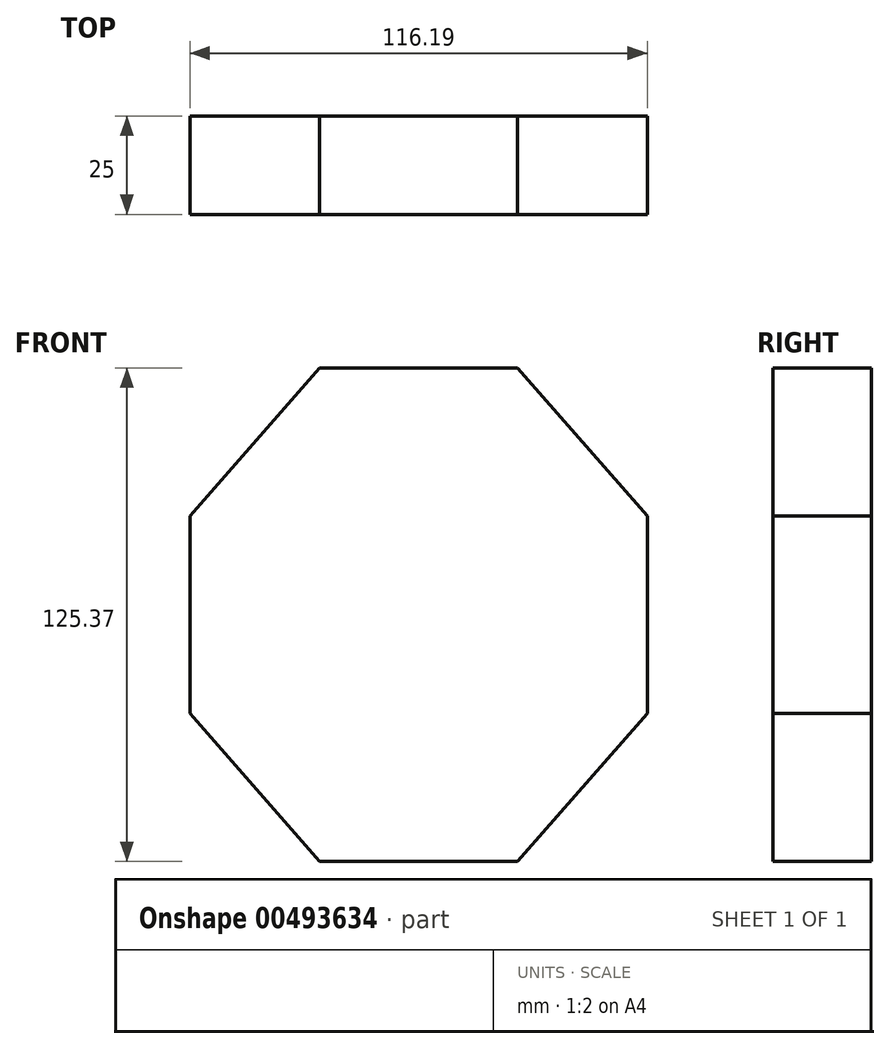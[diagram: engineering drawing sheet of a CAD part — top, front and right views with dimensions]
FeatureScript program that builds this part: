
annotation { "Feature Type Name" : "Feature", "Feature Type Description" : "" }
export const myFeature = defineFeature(function(context is Context, id is Id, definition is map)
    precondition{}
    {
        {
            var Q0;
            Q0=qCreatedBy(makeId("Front.planeOp"),FACE);
            var sketch = newSketch(context, id + "F0", { "sketchPlane" : qUnion([Q0])});
            skLineSegment(sketch, "E0", {"start": v(-37.3, 52.64) * mm, "end": v(12.9, 52.64) * mm});
            skLineSegment(sketch, "E1", {"start": v(12.9, 52.64) * mm, "end": v(45.9, 15.06) * mm});
            skLineSegment(sketch, "E2", {"start": v(45.9, 15.06) * mm, "end": v(45.9, -35.14) * mm});
            skLineSegment(sketch, "E3", {"start": v(45.9, -35.14) * mm, "end": v(12.9, -72.73) * mm});
            skLineSegment(sketch, "E4", {"start": v(12.9, -72.73) * mm, "end": v(-37.3, -72.73) * mm});
            skLineSegment(sketch, "E5", {"start": v(-37.3, -72.73) * mm, "end": v(-70.29, -35.14) * mm});
            skLineSegment(sketch, "E6", {"start": v(-70.29, -35.14) * mm, "end": v(-70.29, 15.06) * mm});
            skLineSegment(sketch, "E7", {"start": v(-70.29, 15.06) * mm, "end": v(-37.3, 52.64) * mm});
            skSolve(sketch);
        }
        {
            var Q0;
            Q0 = qSketchRegion(id + "F0", true);
            extrude(context, id + "F1", {"entities" : qUnion([Q0]), "depth" : 25 * mm});
        }
    });
